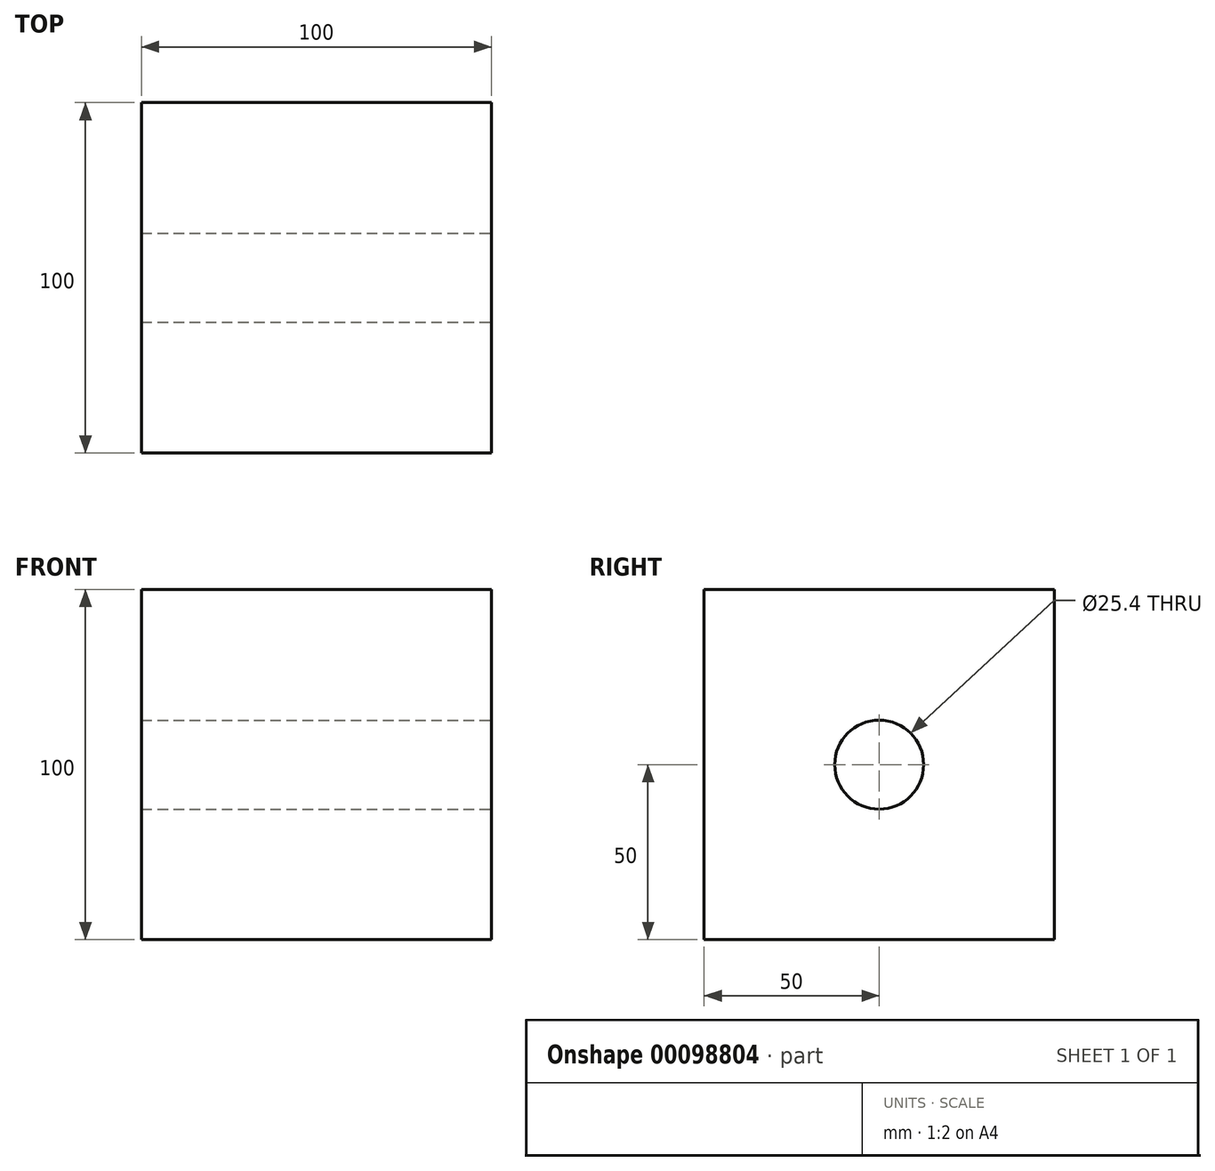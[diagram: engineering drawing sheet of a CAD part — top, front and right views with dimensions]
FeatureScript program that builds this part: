
annotation { "Feature Type Name" : "Feature", "Feature Type Description" : "" }
export const myFeature = defineFeature(function(context is Context, id is Id, definition is map)
    precondition{}
    {
        {
            var Q0;
            Q0=qCreatedBy(makeId("Front.planeOp"),FACE);
            var sketch = newSketch(context, id + "F0", { "sketchPlane" : qUnion([Q0])});
            skLineSegment(sketch, "E0.bottom", {"start": v(50, 50) * mm, "end": v(-50, 50) * mm});
            skLineSegment(sketch, "E0.top", {"start": v(50, -50) * mm, "end": v(-50, -50) * mm});
            skLineSegment(sketch, "E0.left", {"start": v(50, 50) * mm, "end": v(50, -50) * mm});
            skLineSegment(sketch, "E0.right", {"start": v(-50, 50) * mm, "end": v(-50, -50) * mm});
            skPoint(sketch, "E0.middle", {"position": v(0, 0) * mm});
            skSolve(sketch);
        }
        {
            var Q0;
            Q0=makeQuery(id+"F0.imprint","IMPRINT",FACE,{"disambiguationData":[TD([[makeQuery(id+"F0.imprint","IMPRINT",EDGE,{"derivedFrom":sQuery(id+"F0.wireOp",EDGE,"E0.bottom")}),1.0]])]});
            extrude(context, id + "F1", {"entities" : qUnion([Q0]), "depth" : 100 * mm});
        }
        {
            var Q0;
            Q0=makeQuery(id+"F1.opExtrude","SWEPT_FACE",FACE,{"disambiguationData":[OSD([sQuery(id+"F0.wireOp",EDGE,"E0.left")])]});
            var sketch = newSketch(context, id + "F2", { "sketchPlane" : qUnion([Q0])});
            skCircle(sketch, "E1", {"center": v(-50, 0) * mm, "radius": 12.7 * mm});
            skSolve(sketch);
        }
        {
            var Q0;
            Q0 = qSketchRegion(id + "F2", true);
            extrude(context, id + "F3", {"entities" : qUnion([Q0]), "operationType" : NewBodyOperationType.REMOVE, "endBound" : BoundingType.THROUGH_ALL, "oppositeDirection" : true, "depth" : 25 * mm});
        }
    });
